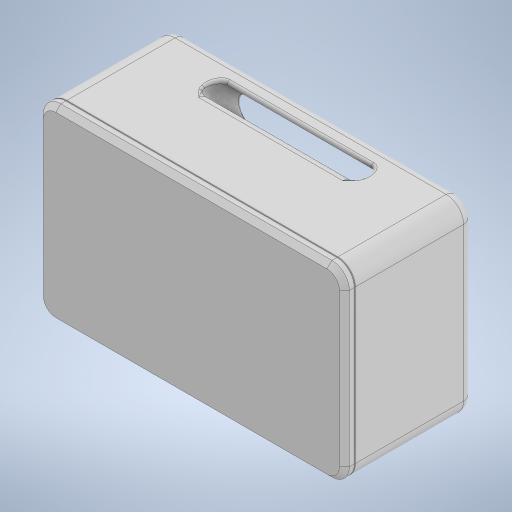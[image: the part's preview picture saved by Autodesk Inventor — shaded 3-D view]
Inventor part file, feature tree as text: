
AUTODESK INVENTOR PART (.ipt)
format: ipt  version: 2024.3 (Build 283343000, 343)  size: 664,576 bytes
history: native  units: in
note: dims shown in document units (in); Inventor stores cm internally (conversion verified against a paired STEP export)
features: other x11, extrude x7, fillet x7, sketch x7, reference x6, projected_geometry x4, chamfer x3, shell x1, plane x1
ambient origin geometry x8: Origin, YZ Plane, XZ Plane, XY Plane, X Axis, Y Axis, Z Axis, Center Point
bodies: Solid1 (feature_tree), Solid2 (feature_tree)
feature tree (47):
  extrude  "Extrusion1"  Depth=1.4882in
  fillet  "Fillet1"  Radius=0.9055in
  extrude  "Extrusion2"  Depth=0.0787in
  fillet  "Fillet2"  Radius=0.1181in
  fillet  "Fillet3"  Radius=1.2598in
  fillet  "Fillet4"  Radius=0.0591in
  shell  "Shell1"  Thickness=0.0197in
  extrude  "Extrusion3"  TaperAngle=45.0deg  [1 undecoded]
  chamfer  "Chamfer1"  Distance=0.0591in
  fillet  "Fillet5"  Radius=0.0157in
  plane  "Work Plane1"
  extrude  "Extrusion4"  Depth=0.0787in
  fillet  "Fillet6"  Radius=0.0787in
  fillet  "Fillet7"  Radius=0.0236in
  extrude  "Extrusion5"  Depth=0.0079in
  extrude  "Extrusion6"  Depth=0.0079in
  extrude  "Extrusion7"  Depth=0.0787in TaperAngle=0.0deg
  other  "Lip1"
  other  "Lip2"
  chamfer  "Chamfer2"  Distance=0.0394in
  sketch  "Sketch1"  dims[d0=2.4252in d1=1.4882in d2=0.9055in d3=0.0in]
  sketch  "Sketch2"  dims[d4=0.1378in d5=0.0787in d8=0.1181in d9=1.2598in d10=0.0in d11=0.0591in d12=0.0197in]
  reference  "Reference3"
  reference  "Reference4"
  sketch  "Sketch3"  dims[d13=0.1378in d14=45.0deg]
  reference  "Reference5"
  sketch  "Sketch4"  dims[d15=0.0591in]
  projected_geometry  "Projected Loop1"
  reference  "Reference6"
  reference  "Reference7"
  other  "Work Point1"
  sketch  "Sketch5"  dims[d19=0.0669in]
  reference  "Reference8"
  sketch  "Sketch6"  dims[d20=0.0669in]
  projected_geometry  "Projected Loop2"
  sketch  "Sketch7"  dims[d21=0.0079in d22=0.0591in d24=0.0157in d25=0.0157in d26=0.0787in d27=0.0in d28=0.0236in d29=0.0079in d30=0.0079in d31=0.0787in d32=0.0in d33=0.0394in d34=0.0787in d35=0.0394in d36=0.0787in d37=45.0deg d38=0.0079in d39=0.0in d40=0.0in d41=0.1181in d42=0.0in d43=0.0591in d44=0.0591in d45=-0.2061in d46=0.0315in d47=0.0315in d48=0.0in d49=0.0in d50=30.0deg d51=0.0in d52=0.0394in d53=0.0394in d54=0.0in d55=0.0in d56=30.0deg d57=0.0in d58=0.0394in d59=0.0787in d60=45.0deg]
  projected_geometry  "Projected Loop3"
  projected_geometry  "Project Cut Edges1"
  other  "<userpath> TUF\Documents\Inventor\ParkinsonDetection\WalkDetection-V1.iam"
  other  "WalkDetection-V1.iam"
  other  "PCB:1"
  other  "PCB-V1:1"
  other  "LP112527-3.7V650mAh:1"
  other  "XIAO-nRF52840 v15:1"
  other  "USB TYPE C PORT:1"
  other  "USB TYPE C PORT (1):1"
  chamfer  "CHAMFER9:1"  Distance=0.0787in
note: 1 required parameter value undecoded (feature->parameter linkage not recoverable at this tier; creation-order binding heuristic only, values carry confidence <= 0.55)
